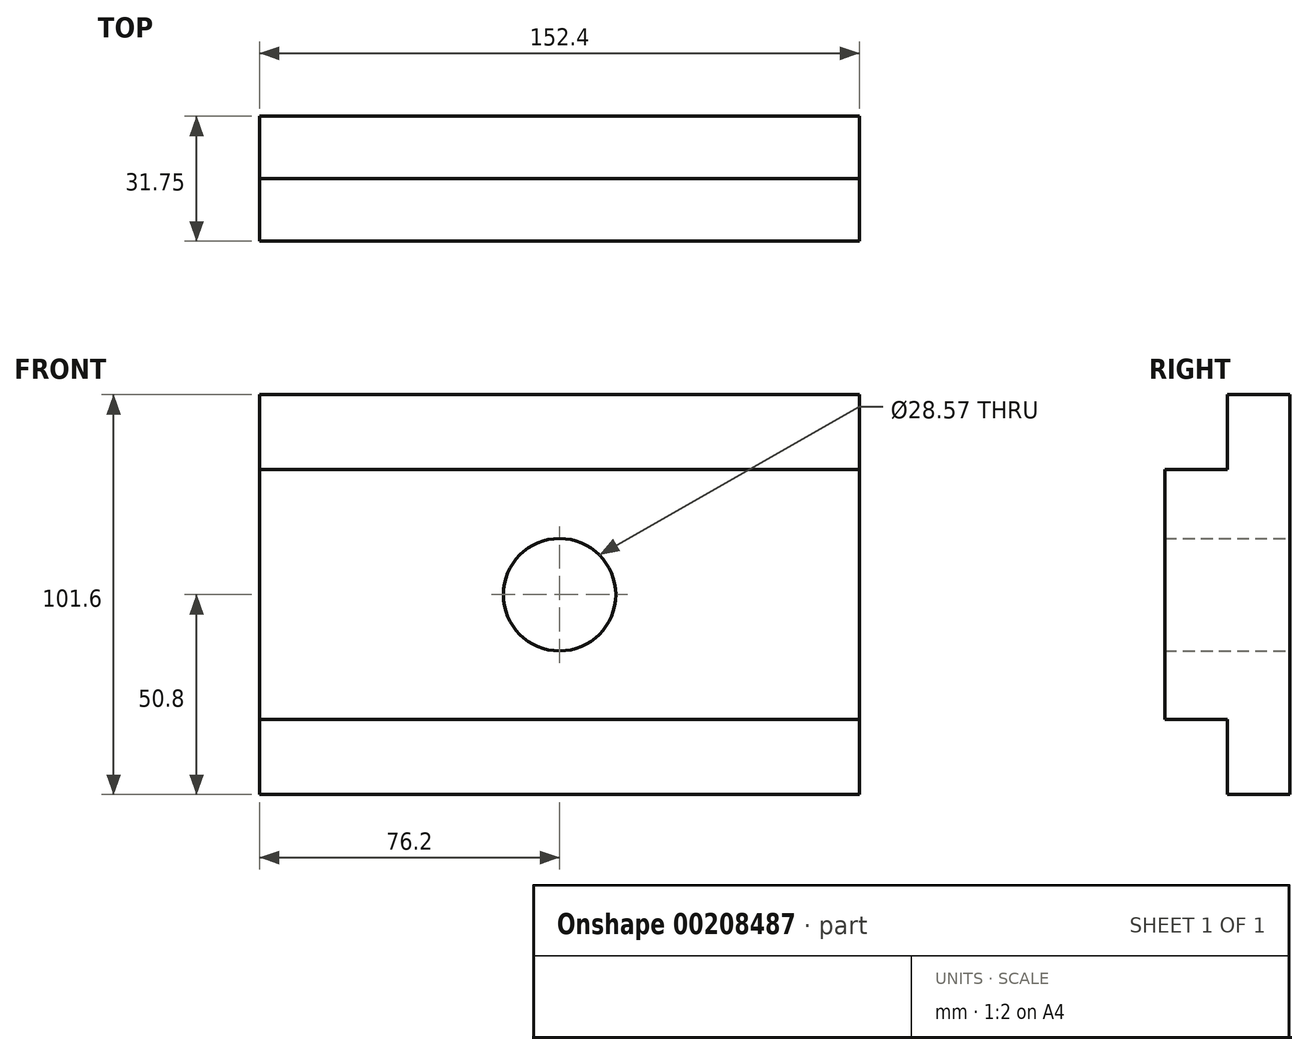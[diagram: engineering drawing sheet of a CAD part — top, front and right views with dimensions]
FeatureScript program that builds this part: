
annotation { "Feature Type Name" : "Feature", "Feature Type Description" : "" }
export const myFeature = defineFeature(function(context is Context, id is Id, definition is map)
    precondition{}
    {
        {
            var Q0;
            Q0=qCreatedBy(makeId("Front.planeOp"),FACE);
            var sketch = newSketch(context, id + "F0", { "sketchPlane" : qUnion([Q0])});
            skPoint(sketch, "E0.start.orphan", {"position": v(-2.32, -3.16) * mm});
            skPoint(sketch, "E1.end.orphan", {"position": v(26.77, -3.16) * mm});
            skPoint(sketch, "E2.end.orphan", {"position": v(-23.4, -11.35) * mm});
            skPoint(sketch, "E2.start.orphan", {"position": v(-23.4, -3.16) * mm});
            skCircle(sketch, "E3", {"center": v(0, 0) * mm, "radius": 14.29 * mm});
            skLineSegment(sketch, "E4", {"start": v(0, 0) * mm, "end": v(0, 31.75) * mm, "construction": true});
            skLineSegment(sketch, "E5", {"start": v(-76.44, 0) * mm, "end": v(77.07, 0) * mm, "construction": true});
            skLineSegment(sketch, "E6.MirrorCS", {"start": v(0, 0) * mm, "end": v(0, -31.75) * mm, "construction": true});
            skLineSegment(sketch, "E7", {"start": v(0, 31.75) * mm, "end": v(-76.2, 31.75) * mm});
            skLineSegment(sketch, "E8.MirrorCS", {"start": v(0, 31.75) * mm, "end": v(76.2, 31.75) * mm});
            skLineSegment(sketch, "E9.MirrorCS", {"start": v(0, -31.75) * mm, "end": v(-76.2, -31.75) * mm});
            skLineSegment(sketch, "E10.MirrorCS", {"start": v(0, -31.75) * mm, "end": v(76.2, -31.75) * mm});
            skLineSegment(sketch, "E11", {"start": v(-76.2, 31.75) * mm, "end": v(-76.2, -31.75) * mm});
            skLineSegment(sketch, "E12", {"start": v(76.2, 31.75) * mm, "end": v(76.2, -31.75) * mm});
            skLineSegment(sketch, "E13", {"start": v(-76.2, 31.75) * mm, "end": v(-76.2, 50.8) * mm});
            skLineSegment(sketch, "E14.MirrorCS", {"start": v(76.2, 31.75) * mm, "end": v(76.2, 50.8) * mm});
            skLineSegment(sketch, "E15.MirrorCS", {"start": v(76.44, 0) * mm, "end": v(-77.07, 0) * mm, "construction": true});
            skLineSegment(sketch, "E16.MirrorCS", {"start": v(-76.2, -31.75) * mm, "end": v(-76.2, -50.8) * mm});
            skLineSegment(sketch, "E17.MirrorCS", {"start": v(76.2, -31.75) * mm, "end": v(76.2, -50.8) * mm});
            skLineSegment(sketch, "E18", {"start": v(-76.2, 50.8) * mm, "end": v(76.2, 50.8) * mm});
            skLineSegment(sketch, "E19", {"start": v(-76.2, -50.8) * mm, "end": v(76.2, -50.8) * mm});
            skSolve(sketch);
        }
        {
            var Q0;
            Q0=makeQuery(id+"F0.imprint","IMPRINT",FACE,{"disambiguationData":[TD([[makeQuery(id+"F0.imprint","IMPRINT",EDGE,{"derivedFrom":sQuery(id+"F0.wireOp",EDGE,"E3")}),-1.0]])]});
            extrude(context, id + "F1", {"entities" : qUnion([Q0]), "depth" : 31.75 * mm});
        }
        {
            var Q0;
            Q0=makeQuery(id+"F0.imprint","IMPRINT",FACE,{"disambiguationData":[TD([[makeQuery(id+"F0.imprint","IMPRINT",EDGE,{"derivedFrom":sQuery(id+"F0.wireOp",EDGE,"E9.MirrorCS")}),1.0]])]});
            var Q1;
            Q1=makeQuery(id+"F0.imprint","IMPRINT",FACE,{"disambiguationData":[TD([[makeQuery(id+"F0.imprint","IMPRINT",EDGE,{"derivedFrom":sQuery(id+"F0.wireOp",EDGE,"E7")}),-1.0]])]});
            extrude(context, id + "F2", {"entities" : qUnion([Q0, Q1]), "operationType" : NewBodyOperationType.ADD, "depth" : 15.88 * mm});
        }
    });
